# Revit family: Shades-Hunter_Douglas-RB500-Single_Standard_Duty-Auto-38_46_55_Bracket
name_source: partatom
category: Specialty Equipment
units: mm (PartAtom-declared; Revit-internal decimal feet)

## family parameters
Always vertical = Yes
Classification Number = 23.30.60.14
Cut with Voids When Loaded = No
Enable Cutting in Views = No
Maintain Annotation Orientation = No
Part Type = Normal
Room Calculation Point = No
Round Connector Dimension = Use Diameter
Shared = No
Work Plane-Based = No

## types (6) — shared parameters
Assembly Code = E2010300
CD_Fabric Sizing Disclaimer = Designer to verify maximum fabric size with Manufacturer as the maximum fabric size is dependent on finished dimensions
CD_Finish = Fabric-Shade-Hunter_Douglas-5%-E_Screen-Charcoal_Cocoa
CD_Finish Frame = Metal-Aluminum-Hunter_Douglas-Anodized-White
CD_Finish Rail = Metal-Aluminum-Hunter_Douglas-Anodized-White
CD_Install Documentation = https://www.hunterdouglasarchitectural.com
CD_Microsite = https://microsite.caddetails.com
CD_Product Documentation Link = https://www.hunterdouglasarchitectural.com
CD_Product Name = RB 500 Roller Shade System
CD_Product Page URL = https://www.hunterdouglasarchitectural.com
CD_Warranty = https://assets.hunterdouglasarchitectural.com
Default Elevation = 0' - 0"
Description = Standard Duty Automatic Roller Shade
Manufacturer = Hunter Douglas Architectural
URL = https://www.hunterdouglasarchitectural.com

## per-type parameters (varying)
| type | CD_38 | CD_46 | CD_55 | CD_Bracket Depth | CD_Bracket Height | CD_Horizontal Roller Offset | CD_Roller Center Line Offset | CD_Screen Offset From Face | CD_Side Mount | CD_Side Mount 38 | CD_Side Mount 46 | CD_Side Mount 55 | CD_Top Mount | CD_Top Mount 38 | CD_Top Mount 46 | CD_Top Mount 55 | Model | Type Comments |
| 38 Side Mounted | Yes | No | No | 0' - 2 19/32" | 0' - 2 19/32" | 0' - 1 5/16" | 0' - 1 1/32" | 0' - 0 17/32" | Yes | Yes | No | No | No | No | No | No | Standard Duty Automated 55 Bracket | Side Mounted |
| 38 Top Mounted | Yes | No | No | 0' - 2 19/32" | 0' - 2 19/32" | 0' - 1 1/32" | 0' - 1 5/16" | 0' - 0 9/32" | No | No | No | No | Yes | Yes | No | No | Standard Duty Automated 55 Bracket | Top Mounted |
| 55 Side Mounted | No | No | Yes | 0' - 3 3/16" | 0' - 3 3/16" | 0' - 1 29/32" | 0' - 0 15/16" | 0' - 1 7/32" | Yes | No | No | Yes | No | No | No | No | Standard Duty Automated 55 Bracket | Side Mounted |
| 55 Top Mounted | No | No | Yes | 0' - 3 3/16" | 0' - 3 3/16" | 0' - 1 3/32" | 0' - 1 19/32" | 0' - 0 17/32" | No | No | No | No | Yes | No | No | Yes | Standard Duty Automated 55 Bracket | Top Mounted |
| 46 Top Mounted | No | Yes | No | 0' - 2 13/16" | 0' - 2 13/16" | 0' - 1 3/32" | 0' - 1 7/32" | 0' - 0 17/32" | No | No | No | No | Yes | No | Yes | No | Standard Duty Automated 46 Bracket | Top Mounted |
| 46 Side Mounted | No | Yes | No | 0' - 2 13/16" | 0' - 2 13/16" | 0' - 1 9/16" | 0' - 1" | 0' - 0 3/4" | Yes | No | Yes | No | No | No | No | No | Standard Duty Automated 46 Bracket | Side Mounted |

## geometry (parser evidence)
native form markers: Sweep x3
no freeform markers — native parametric forms only
